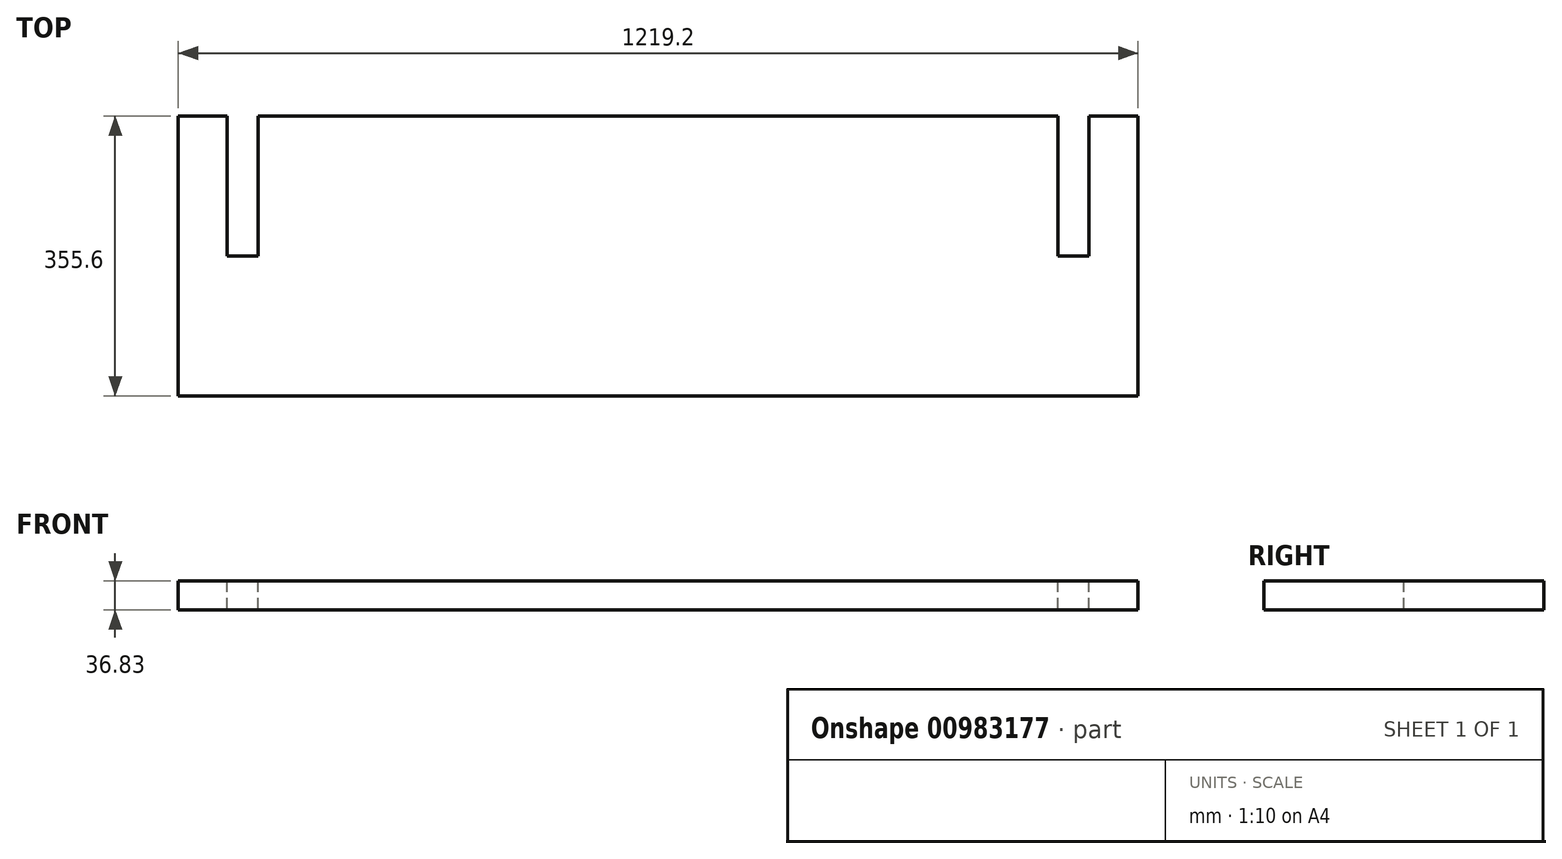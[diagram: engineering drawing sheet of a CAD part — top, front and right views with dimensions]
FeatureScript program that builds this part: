
annotation { "Feature Type Name" : "Feature", "Feature Type Description" : "" }
export const myFeature = defineFeature(function(context is Context, id is Id, definition is map)
    precondition{}
    {
        {
            var Q0;
            Q0=qCreatedBy(makeId("Top.planeOp"),FACE);
            var sketch = newSketch(context, id + "F0", { "sketchPlane" : qUnion([Q0])});
            skLineSegment(sketch, "E0.bottom", {"start": v(609.6, -177.8) * mm, "end": v(-609.6, -177.8) * mm});
            skLineSegment(sketch, "E0.top", {"start": v(609.6, 177.8) * mm, "end": v(-609.6, 177.8) * mm});
            skLineSegment(sketch, "E0.left", {"start": v(609.6, -177.8) * mm, "end": v(609.6, 177.8) * mm});
            skLineSegment(sketch, "E0.right", {"start": v(-609.6, -177.8) * mm, "end": v(-609.6, 177.8) * mm});
            skPoint(sketch, "E0.middle", {"position": v(0, 0) * mm});
            skSolve(sketch);
        }
        {
            var Q0;
            Q0=makeQuery(id+"F0.imprint","IMPRINT",FACE,{"disambiguationData":[TD([[makeQuery(id+"F0.imprint","IMPRINT",EDGE,{"derivedFrom":sQuery(id+"F0.wireOp",EDGE,"E0.bottom")}),-1.0]])]});
            extrude(context, id + "F1", {"entities" : qUnion([Q0]), "depth" : 36.83 * mm, "offsetDistance" : 25.4 * mm});
        }
        {
            var Q0;
            Q0=makeQuery(id+"F1.opExtrude","CAP_FACE",FACE,{"disambiguationData":[OSD([sQuery(id+"F0.wireOp",EDGE,"E0.bottom"),sQuery(id+"F0.wireOp",EDGE,"E0.top"),sQuery(id+"F0.wireOp",EDGE,"E0.left"),sQuery(id+"F0.wireOp",EDGE,"E0.right")])],"isStart":false});
            var sketch = newSketch(context, id + "F2", { "sketchPlane" : qUnion([Q0])});
            skLineSegment(sketch, "E1.bottom", {"start": v(-547.37, 177.8) * mm, "end": v(-508, 177.8) * mm});
            skLineSegment(sketch, "E1.top", {"start": v(-547.37, 0) * mm, "end": v(-508, 0) * mm});
            skLineSegment(sketch, "E1.left", {"start": v(-547.37, 177.8) * mm, "end": v(-547.37, 0) * mm});
            skLineSegment(sketch, "E1.right", {"start": v(-508, 177.8) * mm, "end": v(-508, 0) * mm});
            skLineSegment(sketch, "E2.MirrorCS", {"start": v(547.37, 0) * mm, "end": v(508, 0) * mm});
            skLineSegment(sketch, "E3.MirrorCS", {"start": v(508, 177.8) * mm, "end": v(508, 0) * mm});
            skLineSegment(sketch, "E4.MirrorCS", {"start": v(547.37, 177.8) * mm, "end": v(508, 177.8) * mm});
            skLineSegment(sketch, "E5.MirrorCS", {"start": v(547.37, 177.8) * mm, "end": v(547.37, 0) * mm});
            skSolve(sketch);
        }
        {
            var Q0;
            Q0 = qSketchRegion(id + "F2", true);
            extrude(context, id + "F3", {"entities" : qUnion([Q0]), "operationType" : NewBodyOperationType.REMOVE, "endBound" : BoundingType.UP_TO_NEXT, "oppositeDirection" : true, "depth" : 25.4 * mm, "offsetDistance" : 25.4 * mm});
        }
    });
